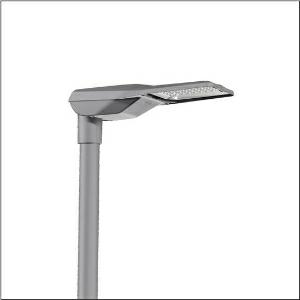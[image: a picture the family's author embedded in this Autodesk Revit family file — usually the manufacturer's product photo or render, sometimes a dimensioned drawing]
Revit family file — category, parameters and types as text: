
# Revit family: streetlight_sl_21_iq_mini___st0_8a_5xe2c41d08gb_f485
name_source: partatom
category: Lighting Fixtures
units: mm (PartAtom-declared; Revit-internal decimal feet)

## family parameters
Cut with Voids When Loaded = No
Host = Face
Light Source = No
Part Type = Normal
Room Calculation Point = No
Round Connector Dimension = Use Diameter
Shared = No

## types (1)
- --- (1 x LED, 5920 lm, 37.1 W, 4000K)
    Apparent Load = 37 VA
    CIE Flux Codes = 38 75 97 100 100
    Color Rendering = 70
    Color Temperature = 4000K
    Default Elevation = 1800 mm
    Description = Streetlight SL 21 mini, mast luminaire, primary light control with lens, of PMMA, primary optical cover: cover, of toughened safety glass, transparent, light distribution: ST0.8a, light emission: direct distribution, primary light characteristic: asymmetric, installation type: post-top, side-entry, LED, High Power LED, rated luminous flux: 5.920lm, luminous efficacy: 160lm/W, light colour: 740, colour temperature: 4000K, control gear: ECG iQ, control: Auto-Match, Temp-Guard, Lumen-Switch, Night-Set, Smart-Wire, Light-Fading, Desk-Remote (wireless, voltage-free reading and setting of iQ features in the workshop via application-optimized NFC function/RFID function), optimised constant luminous flux control (CLO 2.0), mains connection: 220..240V, AC, 50/60Hz, start of lifetime: 37W, end of lifetime: 39W, reduction: 18W, luminaire housing, of diecast aluminium, powder-coated, Siteco® metallic grey (DB 702S), corrosivity category C5 according to DIN EN ISO 12944, length: 628mm, width: 235mm, height: 110mm, spigot size: 60/76mm (post-top) and 42/60/76mm (side-entry), mast flange for spigot size: 42mm: 5XC10008XM4, 60mm: 5XC10008XM2, 76/60mm: 5XC10108XM1, protection rating (complete): IP66, insulation class (complete): insulation class II (safety insulation), certification: CE, ENEC, VDE, impact resistance: IK09, permissible operating ambient temperature for outdoor applications: -40..+50°C, standard-compliant lighting for roads and squares, packaging unit: 1 piece

Light Distribution: ST0.8a
    Height = 110 mm
    Lamp = 1 x LED
    Lamp Light Flux = 5920 lm
    Lamp Power = 37.1 W
    Lamp count = 1
    Length = 625 mm
    Luminous efficacy = 160 lm/W
    Manufacturer = Siteco
    ModVariant = No
    Model = 5XE2C41D08GB
    Number of Poles = 1
    OnlyDefault = Yes
    Power Factor = 1
    Product Name = Streetlight SL 21 iQ mini | ST0.8a
    Product group = mast luminaire | pylon top
    ProductGroupID = 6100
    Protection Class = Protection class II
    Protection Degree = IP 66
    RLX_Detail_Level = 1
    RlxData = <blob elided: 91909 chars, md5=d27949b0>
    Socket = socket
    Standby Power = 0 W
    System Light Flux = 5920 lm
    System Power = 37 W
    Type Comments = factory setting: luminous flux: 100 % | dim-lin: 254 | 385 mA
    Type Image = l_1003519.jpg
    URL = http://relux.com
    VarID = @adj_101885
    Voltage = 0 V
    Weight = 0.00 kg
    Width = 234 mm

## geometry (parser evidence)
native form markers: Blend x4, Sweep x11
no freeform markers — native parametric forms only
